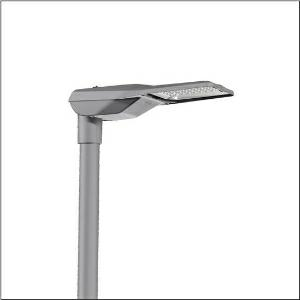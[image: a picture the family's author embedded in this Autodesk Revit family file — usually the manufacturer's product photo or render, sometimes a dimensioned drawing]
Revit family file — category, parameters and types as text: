
# Revit family: streetlight_sl_21_mini___st1_0ab_5xe2m33s08hb_60c9
name_source: partatom
category: Lighting Fixtures
units: mm (PartAtom-declared; Revit-internal decimal feet)

## family parameters
Cut with Voids When Loaded = No
Host = Face
Light Source = No
Part Type = Normal
Room Calculation Point = No
Round Connector Dimension = Use Diameter
Shared = No

## types (1)
- --- (1 x LED, 7960 lm, 66 W, 3000K)
    Apparent Load = 66 VA
    CIE Flux Codes = 38 73 97 100 100
    Color Rendering = 70
    Color Temperature = 3000K
    Default Elevation = 1800 mm
    Description = Streetlight SL 21 mini, mast luminaire, primary light control with lens, of PMMA, primary optical cover: cover, of toughened safety glass, transparent, light distribution: ST1.0aB, light emission: direct distribution, primary light characteristic: asymmetric, installation type: side-entry, post-top, LED, High Power LED, rated luminous flux: 7.960lm, luminous efficacy: 121lm/W, light colour: 730, colour temperature: 3000K, control gear: D4i, control: flexible luminous flux parameterisation, time-dependent luminous flux control, constant luminous flux control, overheat protection, pre-setting: logarithmic dimming characteristic, mains connection: 220..240V, AC, 50/60Hz, start of lifetime: 66W, end of service life: 69W, reduction: 30W, luminaire housing, of diecast aluminium, powder-coated, Siteco® metallic grey (DB 702S), corrosivity category C5 mid according to DIN EN ISO 12944, please order mast flange separately, inclination adjustable: 0°, 5°, 10°, 15°, sealing non-destructively replaceable, multi-level sealing system, length: 628mm, width: 235mm, height: 110mm, mast flange for spigot size: 42mm (side-entry): 5XC10008XM4, 60/48mm (side-entry/post-top): 5XC10108XM2, 76/60mm (side-entry/post-top): 5XC10108XM1, mounting height: 4..8m, Smart Interface above, protection rating (complete): IP66, insulation class (complete): insulation class II (safety insulation), certification: CE, ENEC, ENEC+, VDE, impact resistance: IK10, permissible operating ambient temperature for outdoor applications: -40..+50°C, standard-compliant lighting for roads and squares, packaging unit: 1 piece

Light Distribution: ST1.0aB
    Height = 110 mm
    Lamp = 1 x LED
    Lamp Light Flux = 7960 lm
    Lamp Power = 66 W
    Lamp count = 1
    Length = 625 mm
    Luminous efficacy = 121 lm/W
    Manufacturer = Siteco
    ModVariant = No
    Model = 5XE2M33S08HB
    Number of Poles = 1
    OnlyDefault = Yes
    Power Factor = 1
    Product Name = Streetlight SL 21 mini | ST1.0aB
    Product group = mast luminaire | pylon top
    ProductGroupID = 6100
    Protection Class = Protection class II
    Protection Degree = IP 66
    RLX_Detail_Level = 1
    RLX_Emergency_Light_Flux = 0 lm
    RLX_Emergency_Type = 0
    RLX_Emergency_Type_DB = No
    RlxData = <blob elided: 26077 chars, md5=51bb8068>
    Socket = socket
    Standby Power = 0 W
    System Light Flux = 7960 lm
    System Power = 66 W
    Type Comments = factory setting: luminous flux: 100 % | dim-lin: 254 | 670 mA
    Type Image = l_1003515.jpg
    URL = http://relux.com
    VarID = @adj_203881
    Voltage = 0 V
    Weight = 0.00 kg
    Width = 234 mm

## geometry (parser evidence)
native form markers: Blend x4, Sweep x12
no freeform markers — native parametric forms only
